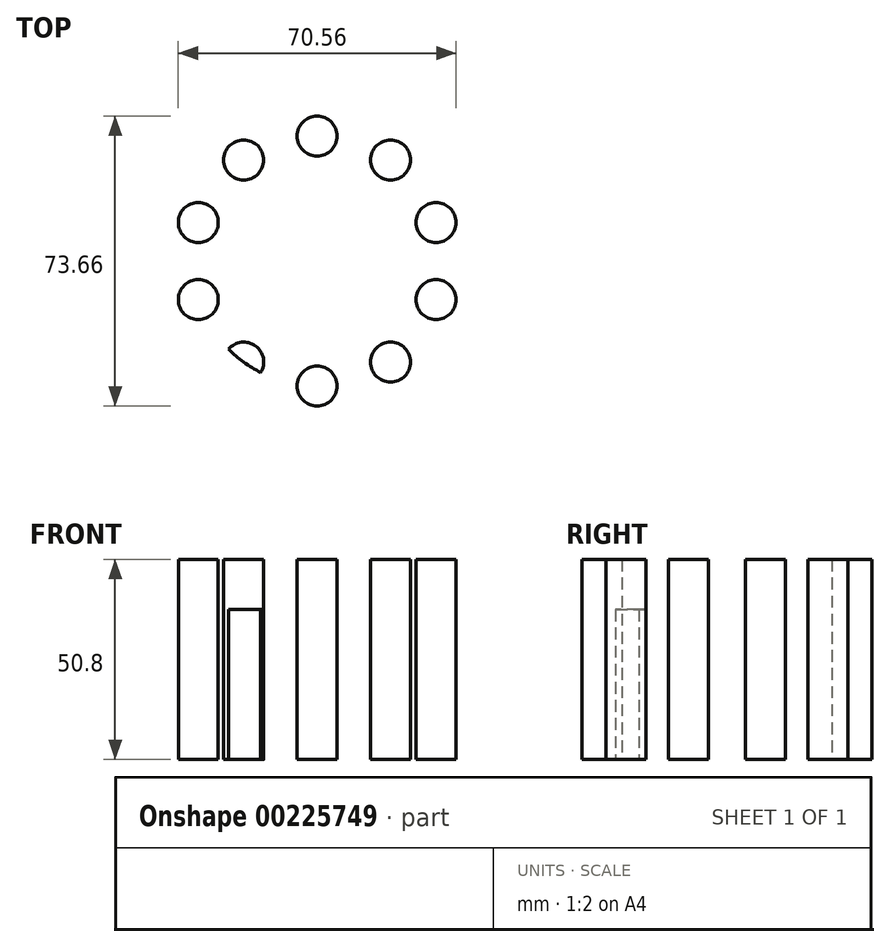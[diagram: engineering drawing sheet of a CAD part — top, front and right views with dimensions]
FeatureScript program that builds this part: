
annotation { "Feature Type Name" : "Feature", "Feature Type Description" : "" }
export const myFeature = defineFeature(function(context is Context, id is Id, definition is map)
    precondition{}
    {
        {
            var Q0;
            Q0=qCreatedBy(makeId("Top.planeOp"),FACE);
            var sketch = newSketch(context, id + "F0", { "sketchPlane" : qUnion([Q0])});
            skCircle(sketch, "E0", {"center": v(0, 0) * mm, "radius": 31.75 * mm});
            skSolve(sketch);
        }
        {
            var Q0;
            Q0=qSketchRegion(id+"F0",true);
            extrude(context, id + "F1", {"entities" : qUnion([Q0]), "depth" : 38.1 * mm});
        }
        {
            var Q0;
            Q0=qCreatedBy(makeId("Top.planeOp"),FACE);
            var sketch = newSketch(context, id + "F2", { "sketchPlane" : qUnion([Q0])});
            skCircle(sketch, "E1", {"center": v(0, 31.75) * mm, "radius": 5.08 * mm});
            skCircle(sketch, "E2.1.0", {"center": v(-18.66, 25.69) * mm, "radius": 5.08 * mm});
            skCircle(sketch, "E2.2.0", {"center": v(-30.2, 9.81) * mm, "radius": 5.08 * mm});
            skCircle(sketch, "E2.3.0", {"center": v(-30.2, -9.81) * mm, "radius": 5.08 * mm});
            skCircle(sketch, "E2.4.0", {"center": v(-18.66, -25.69) * mm, "radius": 5.08 * mm});
            skCircle(sketch, "E2.5.0", {"center": v(0, -31.75) * mm, "radius": 5.08 * mm});
            skCircle(sketch, "E2.6.0", {"center": v(18.66, -25.69) * mm, "radius": 5.08 * mm});
            skCircle(sketch, "E2.7.0", {"center": v(30.2, -9.81) * mm, "radius": 5.08 * mm});
            skCircle(sketch, "E2.8.0", {"center": v(30.2, 9.81) * mm, "radius": 5.08 * mm});
            skCircle(sketch, "E2.9.0", {"center": v(18.66, 25.69) * mm, "radius": 5.08 * mm});
            skPoint(sketch, "E2.center", {"position": v(0, 0) * mm});
            skSolve(sketch);
        }
        {
            var Q0;
            Q0=qSketchRegion(id+"F2",true);
            extrude(context, id + "F3", {"entities" : qUnion([Q0]), "depth" : 50.8 * mm});
        }
        {
            var Q0;
            Q0=makeQuery(id+"F1.opExtrude","SWEPT_BODY",BODY,{"disambiguationData":[OSD([sQuery(id+"F0.wireOp",EDGE,"E0")])]});
            var Q1;
            Q1=makeQuery(id+"F3.opExtrude","SWEPT_BODY",BODY,{"disambiguationData":[OSD([sQuery(id+"F2.wireOp",EDGE,"E1")])]});
            var Q2;
            Q2=makeQuery(id+"F3.opExtrude","SWEPT_BODY",BODY,{"disambiguationData":[OSD([sQuery(id+"F2.wireOp",EDGE,"E2.1.0")])]});
            var Q3;
            Q3=makeQuery(id+"F3.opExtrude","SWEPT_BODY",BODY,{"disambiguationData":[OSD([sQuery(id+"F2.wireOp",EDGE,"E2.2.0")])]});
            var Q4;
            Q4=makeQuery(id+"F3.opExtrude","SWEPT_BODY",BODY,{"disambiguationData":[OSD([sQuery(id+"F2.wireOp",EDGE,"E2.3.0")])]});
            var Q5;
            Q5=makeQuery(id+"F3.opExtrude","SWEPT_BODY",BODY,{"disambiguationData":[OSD([sQuery(id+"F2.wireOp",EDGE,"E2.4.0")])]});
            var Q6;
            Q6=makeQuery(id+"F3.opExtrude","SWEPT_BODY",BODY,{"disambiguationData":[OSD([sQuery(id+"F2.wireOp",EDGE,"E2.5.0")])]});
            var Q7;
            Q7=makeQuery(id+"F3.opExtrude","SWEPT_BODY",BODY,{"disambiguationData":[OSD([sQuery(id+"F2.wireOp",EDGE,"E2.6.0")])]});
            var Q8;
            Q8=makeQuery(id+"F3.opExtrude","SWEPT_BODY",BODY,{"disambiguationData":[OSD([sQuery(id+"F2.wireOp",EDGE,"E2.7.0")])]});
            var Q9;
            Q9=makeQuery(id+"F3.opExtrude","SWEPT_BODY",BODY,{"disambiguationData":[OSD([sQuery(id+"F2.wireOp",EDGE,"E2.8.0")])]});
            var Q10;
            Q10=makeQuery(id+"F3.opExtrude","SWEPT_BODY",BODY,{"disambiguationData":[OSD([sQuery(id+"F2.wireOp",EDGE,"E2.9.0")])]});
            booleanBodies(context, id + "F4", {"operationType" : BooleanOperationType.INTERSECTION, "tools" : qUnion([Q0, Q1, Q2, Q3, Q4, Q5, Q6, Q7, Q8, Q9, Q10]), "keepTools" : true});
        }
        {
            var Q0;
            Q0=makeQuery(id+"F3.opExtrude","SWEPT_BODY",BODY,{"disambiguationData":[OSD([sQuery(id+"F2.wireOp",EDGE,"E2.4.0")])]});
            var Q1;
            Q1=makeQuery(id+"F1.opExtrude","SWEPT_BODY",BODY,{"disambiguationData":[OSD([sQuery(id+"F0.wireOp",EDGE,"E0")])]});
            booleanBodies(context, id + "F5", {"operationType" : BooleanOperationType.INTERSECTION, "tools" : qUnion([Q0, Q1])});
        }
    });
